# Revit family: A
name_source: partatom
category: Plumbing Fixtures
units: mm (PartAtom-declared; Revit-internal decimal feet)

## family parameters
Cut with Voids When Loaded = No
Host = Face
OmniClass Number = 23.31.11.00
Part Type = Normal
Room Calculation Point = No
Round Connector Dimension = Use Diameter
Shared = No

## types (1)
- 0.5 GPM, CP-Polished Chrome
    ADA Compliant = No
    Assembly Code = D2010
    CW Connection = No
    Cold Water Inlet = Cold Water Inlet
    Date Modified = 02/28/2024
    Default Elevation = 36"
    Description = TB S Deck Mount 0.5 GPM DC With Mixer
    Drain Included = Yes
    Finish = Kohler-Metal-CP-Polished_Chrome
    Flow Rate = 1 GPM
    HW Connection = Yes
    Height = 8 3/8"
    Hot Water Inlet = Hot Water Inlet
    Length = 5 3/4"
    Manufacturer = Kohler Co.
    Master Format 2014 = 22 41 39
    Master Format 2014 Name = Residential Faucets, Supplies, and Trim
    Material = Premium Metal Construction
    Model = K-104MT77-SANA -CP
    Pressure = 0.00 psi
    Product Documentation Link = https://www.us.kohler.com _spec_US-CA_Kohler_en.pdf
    Product Name = Components
    Product Page URL = http://www.us.kohler.com
    Spout Reach = 5 3/4"
    Tempered Water Inlet = Tempered Water Inlet
    Type = 1
    URL = https://www.us.kohler.com
    Vent Connection = No
    Waste Connection = No
    Waste Water Outlet = Waste Water Outlet
    WaterSense Certified = No
    Width = 2 3/8"

## geometry (parser evidence)
native form markers: Sweep x5
no freeform markers — native parametric forms only
